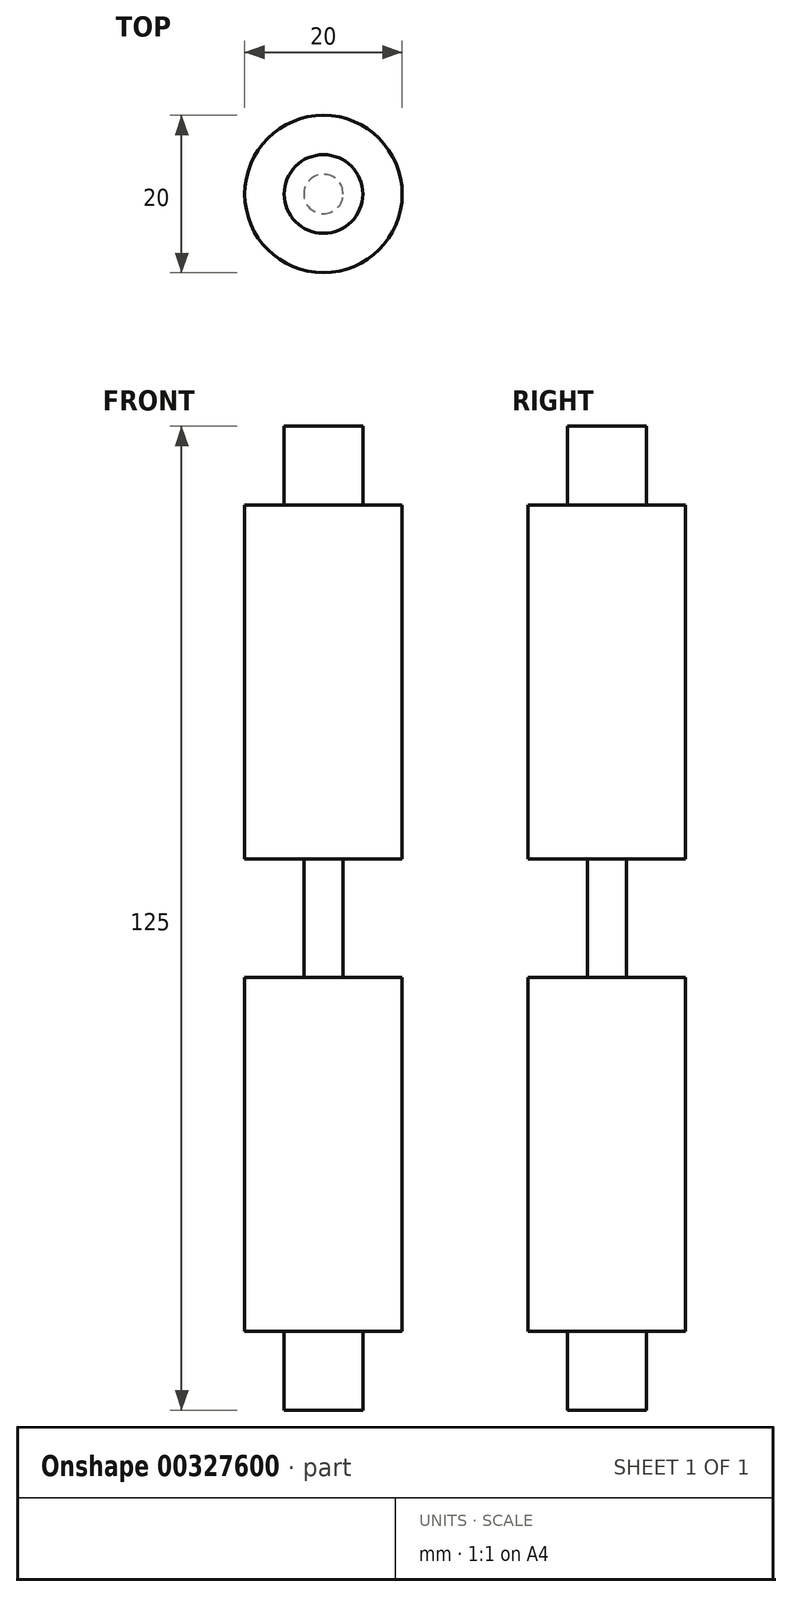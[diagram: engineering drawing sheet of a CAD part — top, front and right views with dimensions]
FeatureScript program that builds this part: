
annotation { "Feature Type Name" : "Feature", "Feature Type Description" : "" }
export const myFeature = defineFeature(function(context is Context, id is Id, definition is map)
    precondition{}
    {
        {
            var Q0;
            Q0=qCreatedBy(makeId("Front.planeOp"),FACE);
            var sketch = newSketch(context, id + "F0", { "sketchPlane" : qUnion([Q0])});
            skLineSegment(sketch, "E0", {"start": v(-2.5, 0) * mm, "end": v(-2.5, 7.5) * mm});
            skLineSegment(sketch, "E1", {"start": v(-2.5, 7.5) * mm, "end": v(-10, 7.5) * mm});
            skLineSegment(sketch, "E2", {"start": v(-10, 7.5) * mm, "end": v(-10, 52.5) * mm});
            skLineSegment(sketch, "E3", {"start": v(-10, 52.5) * mm, "end": v(-5, 52.5) * mm});
            skLineSegment(sketch, "E4", {"start": v(-5, 52.5) * mm, "end": v(-5, 62.5) * mm});
            skLineSegment(sketch, "E5", {"start": v(-5, 62.5) * mm, "end": v(0, 62.5) * mm});
            skLineSegment(sketch, "E6", {"start": v(0, 0) * mm, "end": v(0, 62.5) * mm});
            skLineSegment(sketch, "E7.MirrorCS", {"start": v(-2.5, 0) * mm, "end": v(-2.5, -7.5) * mm});
            skLineSegment(sketch, "E8.MirrorCS", {"start": v(0, 0) * mm, "end": v(0, -62.5) * mm});
            skLineSegment(sketch, "E9.MirrorCS", {"start": v(-2.5, -7.5) * mm, "end": v(-10, -7.5) * mm});
            skLineSegment(sketch, "E10.MirrorCS", {"start": v(-10, -7.5) * mm, "end": v(-10, -52.5) * mm});
            skLineSegment(sketch, "E11.MirrorCS", {"start": v(-10, -52.5) * mm, "end": v(-5, -52.5) * mm});
            skLineSegment(sketch, "E12.MirrorCS", {"start": v(-5, -52.5) * mm, "end": v(-5, -62.5) * mm});
            skLineSegment(sketch, "E13.MirrorCS", {"start": v(-5, -62.5) * mm, "end": v(0, -62.5) * mm});
            skSolve(sketch);
        }
        {
            var Q0;
            Q0=makeQuery(id+"F0.imprint","IMPRINT",FACE,{"disambiguationData":[TD([[makeQuery(id+"F0.imprint","IMPRINT",EDGE,{"derivedFrom":sQuery(id+"F0.wireOp",EDGE,"E0")}),-1.0]])]});
            var Q1;
            Q1=sQuery(id+"F0.wireOp",EDGE,"E6");
            revolve(context, id + "F1", {"entities" : qUnion([Q0]), "axis" : qUnion([Q1]), "revolveType" : RevolveType.FULL});
        }
    });
